# Revit family: Toilet_Seat-Elongated_Closed_Front-KOHLER-PureWarmth_Quiet-Close-K-10349_1
name_source: partatom
category: Specialty Equipment
revit_build: Autodesk Revit 2017 (Build: 20160225_1515(x64)
units: mm (PartAtom-declared; Revit-internal decimal feet)

## family parameters
Cut with Voids When Loaded = No
Host = Face
OmniClass Number = 23.31.25.00
OmniClass Title = Toilet and Bath Specialties
Part Type = Normal
Room Calculation Point = No
Round Connector Dimension = Use Diameter
Shared = No

## types (2) — shared parameters
ADA Compliant = No
Apparent Load = 72 VA
Assembly Code = C1030200
Date Modified = 08/07/2020
Default Elevation = 0"
Description = Heated elongated toilet seat with LED nightlight
Electrical Connector = Yes
Electrical Note = One Dedicated Circuit Required, Protected With Class A Ground-Fault Circuit-Interrupter (GFCI). Outside North America,
This Device May Be Known As a Residual Current Device (RCD).
Height = 1 3/16"
Length = 18 3/4"
Manufacturer = KOHLER Co.
Master Format 2014 = 10 28 00
Master Format 2014 Name = Toilet, Bath, and Laundry Accessories
Material = Plastic
Product Documentation Link = https://www.us.kohler.com
Product Name = PureWarmth Quiet-Close
Product Page URL = http://www.us.kohler.com
Seat Mounting Holes = 5 1/2"
URL = https://www.us.kohler.com
Voltage = 120 V
WaterSense Certified = No
Width = 14 7/8"

## per-type parameters (varying)
| type | Finish | Model | Type |
| 0-White | Kohler-Plastic-0-White | K-10349-0 | 1 |
| 96-Biscuit | Kohler-Plastic-96-Biscuit | K-10349-96 | 2 |

## geometry (parser evidence)
native form markers: Sweep x5
no freeform markers — native parametric forms only
